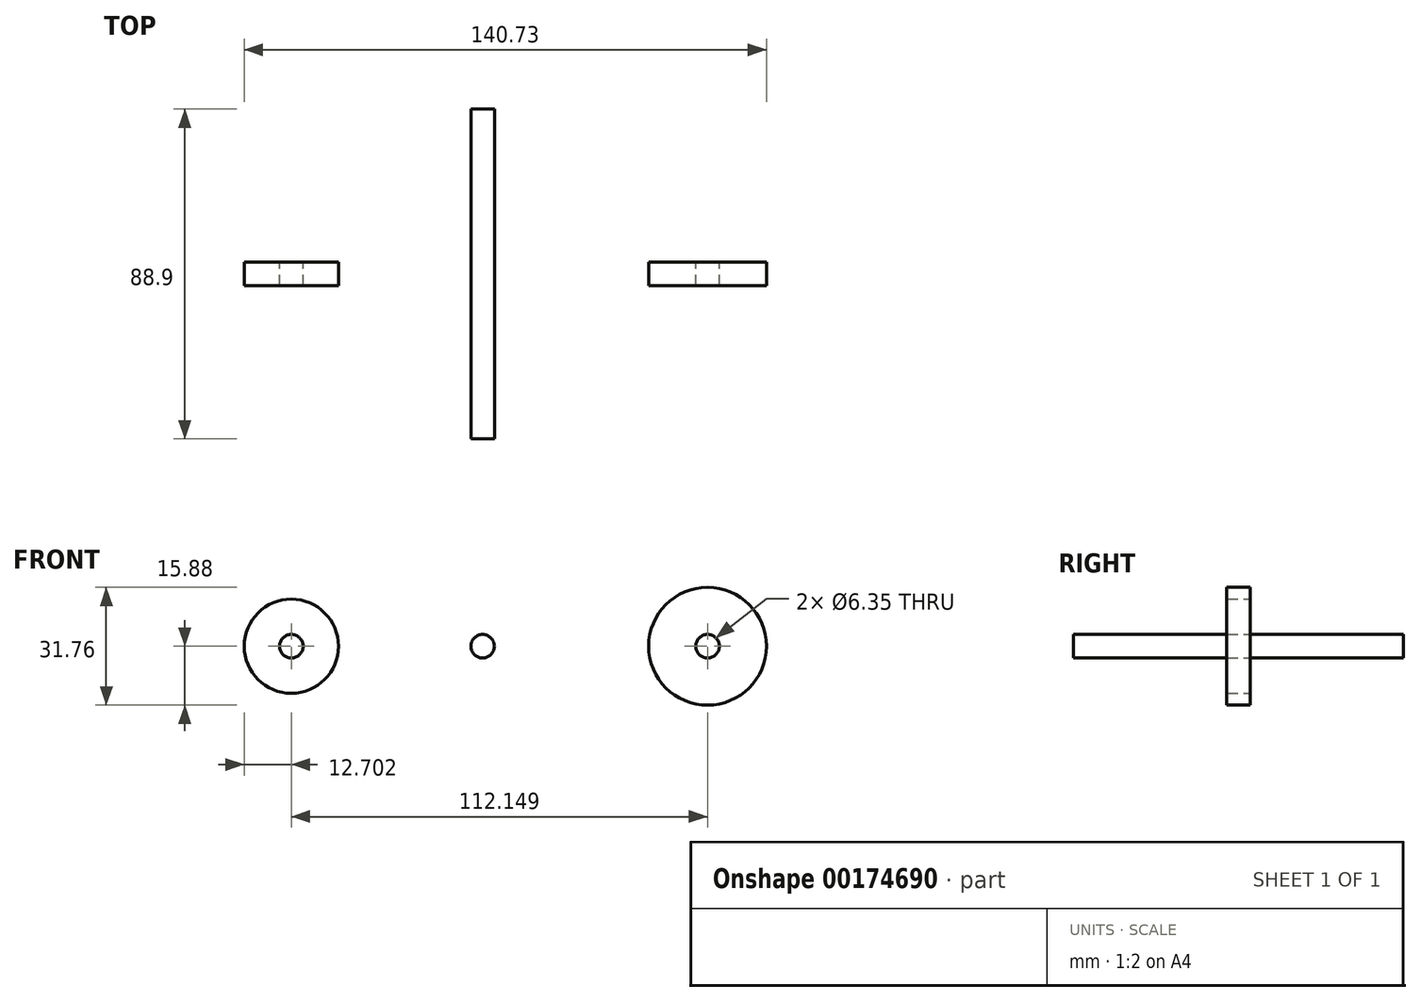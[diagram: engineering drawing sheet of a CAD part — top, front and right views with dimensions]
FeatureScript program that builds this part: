
annotation { "Feature Type Name" : "Feature", "Feature Type Description" : "" }
export const myFeature = defineFeature(function(context is Context, id is Id, definition is map)
    precondition{}
    {
        {
            var Q0;
            Q0=qCreatedBy(makeId("Front.planeOp"),FACE);
            var sketch = newSketch(context, id + "F0", { "sketchPlane" : qUnion([Q0])});
            skCircle(sketch, "E0", {"center": v(0, 0) * mm, "radius": 3.18 * mm});
            skCircle(sketch, "E1", {"center": v(-51.54, 0) * mm, "radius": 12.7 * mm});
            skCircle(sketch, "E2", {"center": v(60.61, 0) * mm, "radius": 15.88 * mm});
            skCircle(sketch, "E3", {"center": v(-51.54, 0) * mm, "radius": 3.18 * mm});
            skCircle(sketch, "E4", {"center": v(60.61, 0) * mm, "radius": 3.18 * mm});
            skSolve(sketch);
        }
        {
            var Q0;
            Q0=makeQuery(id+"F0.imprint","IMPRINT",FACE,{"disambiguationData":[TD([[makeQuery(id+"F0.imprint","IMPRINT",EDGE,{"derivedFrom":sQuery(id+"F0.wireOp",EDGE,"E1")}),1.0]])]});
            var Q1;
            Q1=makeQuery(id+"F0.imprint","IMPRINT",FACE,{"disambiguationData":[TD([[makeQuery(id+"F0.imprint","IMPRINT",EDGE,{"derivedFrom":sQuery(id+"F0.wireOp",EDGE,"E2")}),1.0]])]});
            extrude(context, id + "F1", {"entities" : qUnion([Q0, Q1]), "endBound" : BoundingType.SYMMETRIC, "depth" : 6.35 * mm});
        }
        {
            var Q0;
            Q0=makeQuery(id+"F0.imprint","IMPRINT",FACE,{"disambiguationData":[TD([[makeQuery(id+"F0.imprint","IMPRINT",EDGE,{"derivedFrom":sQuery(id+"F0.wireOp",EDGE,"E0")}),1.0]])]});
            extrude(context, id + "F2", {"entities" : qUnion([Q0]), "endBound" : BoundingType.SYMMETRIC, "depth" : 88.9 * mm});
        }
    });
